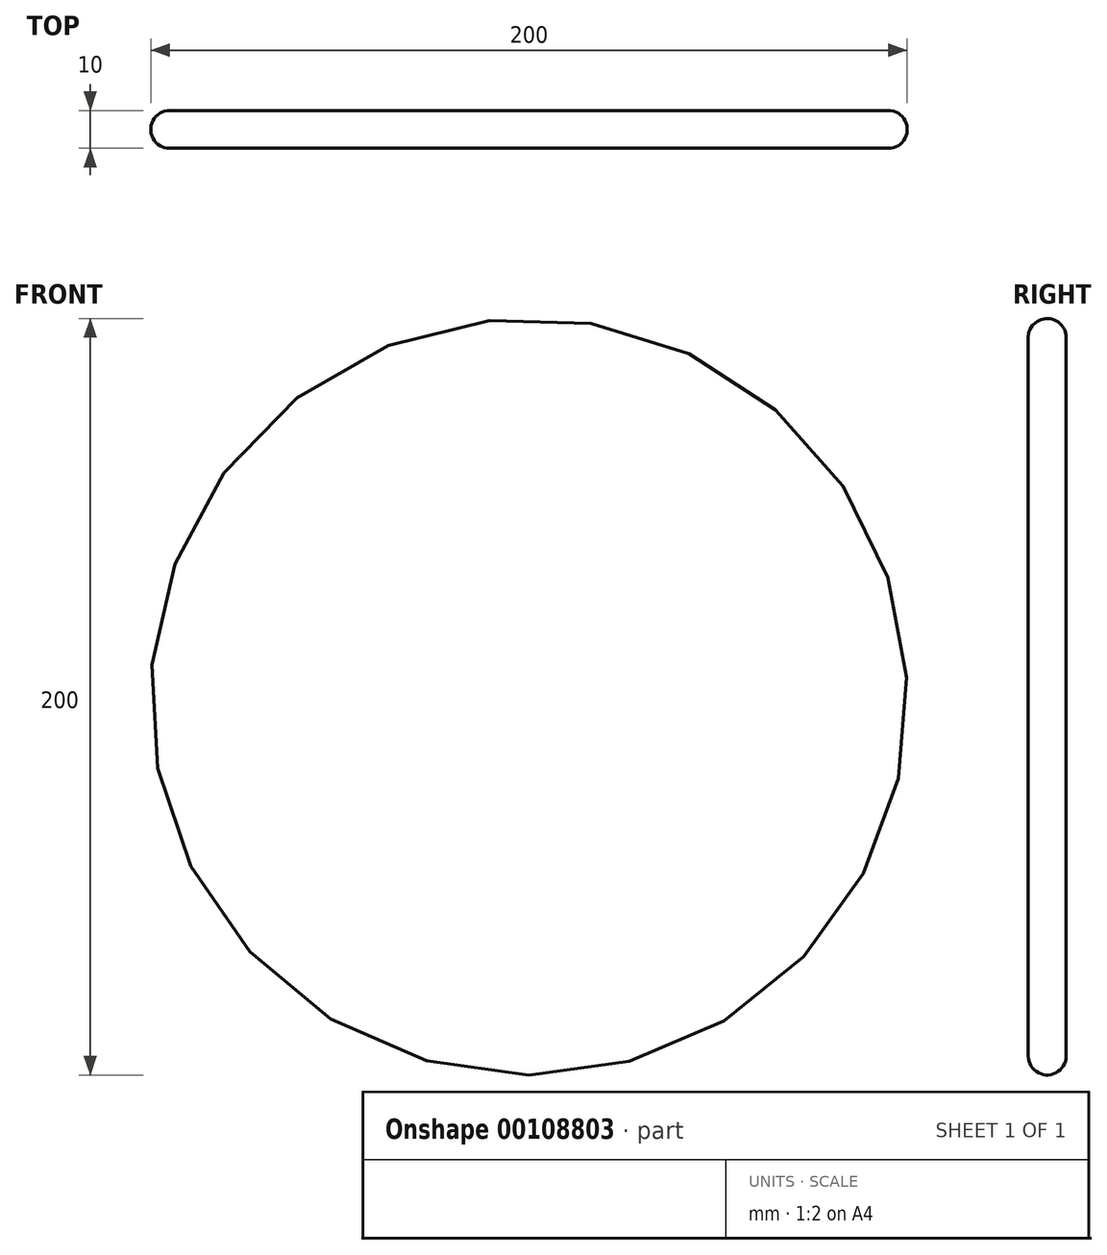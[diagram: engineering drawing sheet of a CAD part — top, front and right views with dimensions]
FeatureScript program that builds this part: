
annotation { "Feature Type Name" : "Feature", "Feature Type Description" : "" }
export const myFeature = defineFeature(function(context is Context, id is Id, definition is map)
    precondition{}
    {
        {
            var Q0;
            Q0=qCreatedBy(makeId("Front.planeOp"),FACE);
            var sketch = newSketch(context, id + "F0", { "sketchPlane" : qUnion([Q0])});
            skCircle(sketch, "E0", {"center": v(0, 0) * mm, "radius": 100 * mm});
            skSolve(sketch);
        }
        {
            var Q0;
            Q0 = qSketchRegion(id + "F0", true);
            extrude(context, id + "F1", {"entities" : qUnion([Q0]), "endBound" : BoundingType.SYMMETRIC, "depth" : 10 * mm});
        }
        {
            var Q0;
            Q0=makeQuery(id+"F1.opExtrude","CAP_EDGE",EDGE,{"disambiguationData":[OSD([sQuery(id+"F0.wireOp",EDGE,"E0")])],"isStart":false});
            var Q1;
            Q1=makeQuery(id+"F1.opExtrude","CAP_EDGE",EDGE,{"disambiguationData":[OSD([sQuery(id+"F0.wireOp",EDGE,"E0")])],"isStart":true});
            fillet(context, id + "F2", {"entities" : qUnion([Q0, Q1]), "radius" : 5 * mm, "tangentPropagation" : true, "allowEdgeOverflow" : false});
        }
    });
